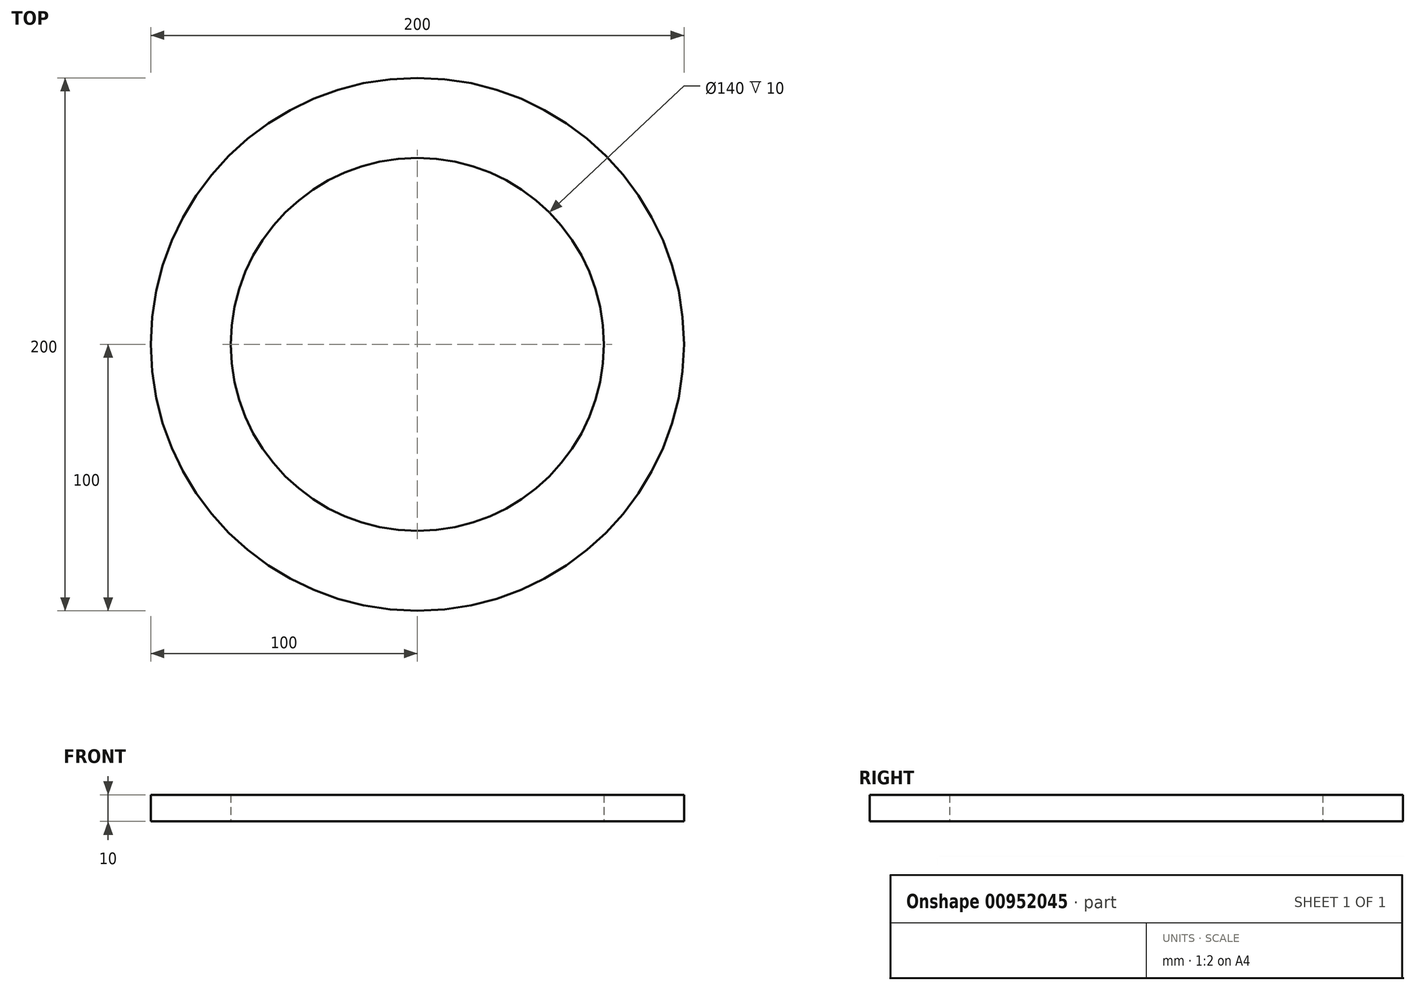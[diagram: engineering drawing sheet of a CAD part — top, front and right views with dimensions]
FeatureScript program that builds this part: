
annotation { "Feature Type Name" : "Feature", "Feature Type Description" : "" }
export const myFeature = defineFeature(function(context is Context, id is Id, definition is map)
    precondition{}
    {
        {
            var Q0;
            Q0=qCreatedBy(makeId("Top.planeOp"),FACE);
            var sketch = newSketch(context, id + "F0", { "sketchPlane" : qUnion([Q0])});
            skCircle(sketch, "E0", {"center": v(0, 0) * mm, "radius": 100 * mm});
            skCircle(sketch, "E1", {"center": v(0, 0) * mm, "radius": 70 * mm});
            skSolve(sketch);
        }
        {
            var Q0;
            Q0 = qSketchRegion(id + "F0", true);
            extrude(context, id + "F1", {"entities" : qUnion([Q0]), "depth" : 10 * mm, "offsetDistance" : 25 * mm});
        }
    });
